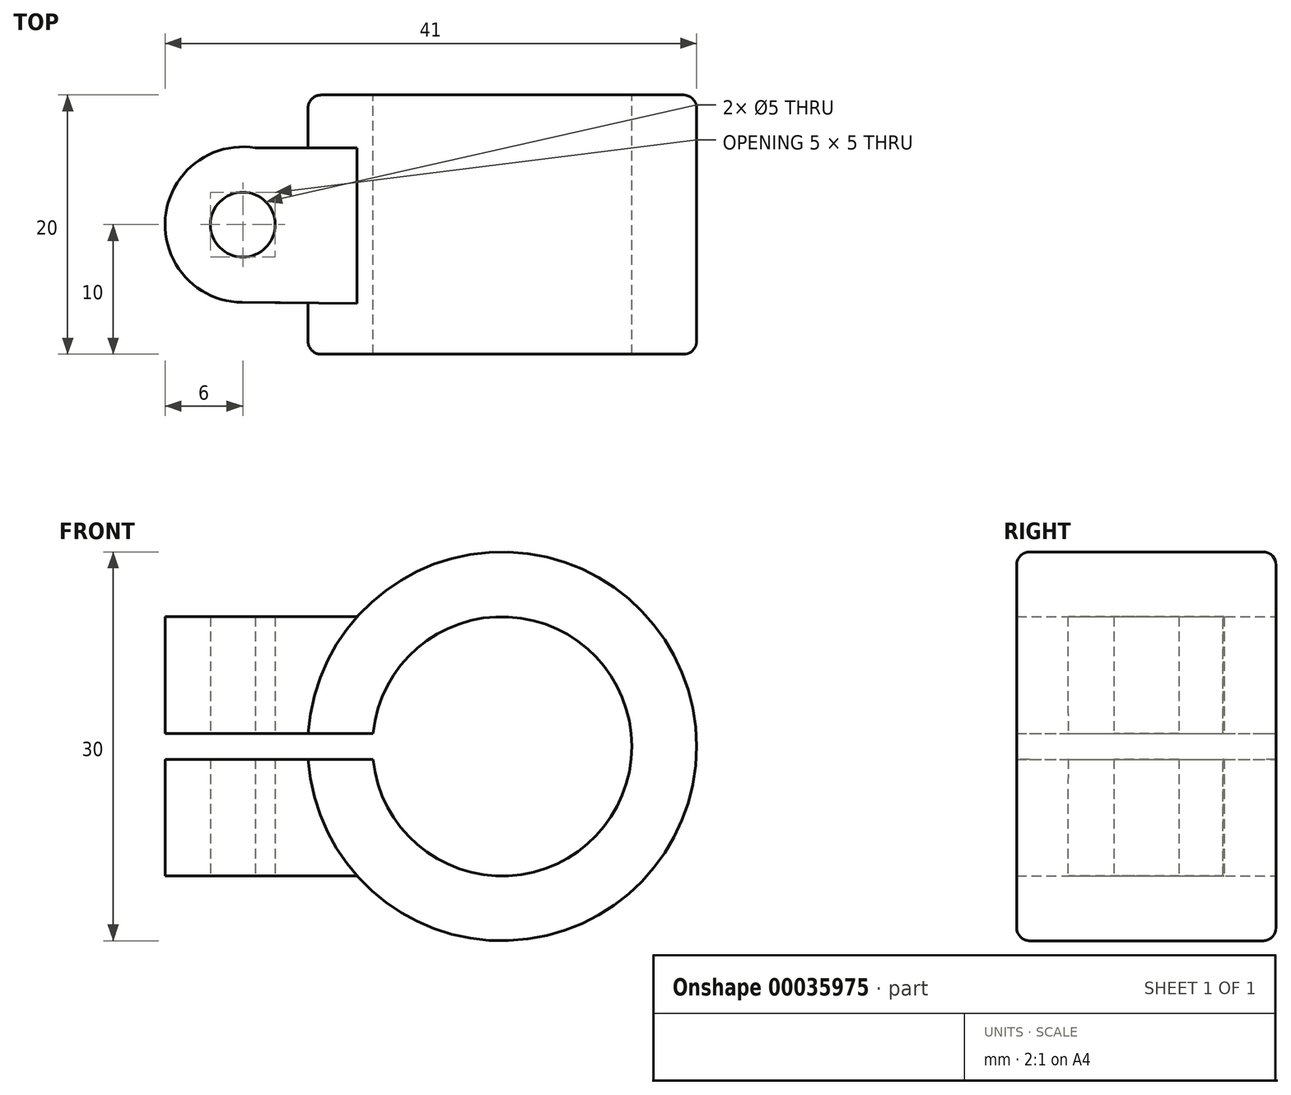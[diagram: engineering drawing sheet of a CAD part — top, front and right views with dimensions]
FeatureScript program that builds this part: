
annotation { "Feature Type Name" : "Feature", "Feature Type Description" : "" }
export const myFeature = defineFeature(function(context is Context, id is Id, definition is map)
    precondition{}
    {
        {
            var Q0;
            Q0=qCreatedBy(makeId("Front.planeOp"),FACE);
            var sketch = newSketch(context, id + "F0", { "sketchPlane" : qUnion([Q0])});
            skCircle(sketch, "E0", {"center": v(0, 0) * mm, "radius": 10 * mm});
            skCircle(sketch, "E1", {"center": v(0, 0) * mm, "radius": 15 * mm});
            skSolve(sketch);
        }
        {
            var Q0;
            Q0=makeQuery(id+"F0.imprint","IMPRINT",FACE,{"disambiguationData":[TD([[makeQuery(id+"F0.imprint","IMPRINT",EDGE,{"derivedFrom":sQuery(id+"F0.wireOp",EDGE,"E0")}),-1.0]])]});
            extrude(context, id + "F1", {"entities" : qUnion([Q0]), "depth" : 10 * mm, "hasSecondDirection" : true, "secondDirectionOppositeDirection" : true, "secondDirectionDepth" : 10 * mm});
        }
        {
            var Q0;
            Q0=qCreatedBy(makeId("Top.planeOp"),FACE);
            var sketch = newSketch(context, id + "F2", { "sketchPlane" : qUnion([Q0])});
            skCircle(sketch, "E2", {"center": v(-20, 0) * mm, "radius": 2.5 * mm});
            skArc(sketch, "E3", {"start": v(-19.04, 5.92) * mm, "mid": v(-25.98, 0.5) * mm, "end": v(-20.05, -6) * mm});
            skLineSegment(sketch, "E4", {"start": v(-19.04, 5.92) * mm, "end": v(-11, 5.92) * mm});
            skLineSegment(sketch, "E5", {"start": v(-11, 5.92) * mm, "end": v(-11, -6.08) * mm});
            skLineSegment(sketch, "E6", {"start": v(-11, -6.08) * mm, "end": v(-20.05, -6) * mm});
            skPoint(sketch, "E7.orphan", {"position": v(-11, 0) * mm});
            skSolve(sketch);
        }
        {
            var Q0;
            Q0=makeQuery(id+"F2.imprint","IMPRINT",FACE,{"disambiguationData":[TD([[makeQuery(id+"F2.imprint","IMPRINT",EDGE,{"derivedFrom":sQuery(id+"F2.wireOp",EDGE,"E2")}),-1.0]])]});
            extrude(context, id + "F3", {"entities" : qUnion([Q0]), "operationType" : NewBodyOperationType.ADD, "depth" : 10 * mm, "hasSecondDirection" : true, "secondDirectionOppositeDirection" : true, "secondDirectionDepth" : 10 * mm});
        }
        {
            var Q0;
            Q0=qCreatedBy(makeId("Front.planeOp"),FACE);
            var sketch = newSketch(context, id + "F4", { "sketchPlane" : qUnion([Q0])});
            skLineSegment(sketch, "E8.bottom", {"start": v(-56.6, 1) * mm, "end": v(-6.6, 1) * mm});
            skLineSegment(sketch, "E8.top", {"start": v(-56.6, -1) * mm, "end": v(-6.6, -1) * mm});
            skLineSegment(sketch, "E8.left", {"start": v(-56.6, 1) * mm, "end": v(-56.6, -1) * mm});
            skLineSegment(sketch, "E8.right", {"start": v(-6.6, 1) * mm, "end": v(-6.6, -1) * mm});
            skSolve(sketch);
        }
        {
            var Q0;
            Q0=makeQuery(id+"F4.imprint","IMPRINT",FACE,{"disambiguationData":[TD([[makeQuery(id+"F4.imprint","IMPRINT",EDGE,{"derivedFrom":sQuery(id+"F4.wireOp",EDGE,"E8.bottom")}),-1.0]])]});
            extrude(context, id + "F5", {"entities" : qUnion([Q0]), "operationType" : NewBodyOperationType.REMOVE, "oppositeDirection" : true, "depth" : 25 * mm, "hasSecondDirection" : true, "secondDirectionOppositeDirection" : false, "secondDirectionDepth" : 25 * mm});
        }
        {
            var Q0;
            Q0=makeQuery(id+"F1.opExtrude","CAP_EDGE",EDGE,{"disambiguationData":[OSD([sQuery(id+"F0.wireOp",EDGE,"E1")])],"isStart":false});
            var Q1;
            Q1=makeQuery(id+"F1.opExtrude","CAP_EDGE",EDGE,{"disambiguationData":[OSD([sQuery(id+"F0.wireOp",EDGE,"E1")])],"isStart":true});
            fillet(context, id + "F6", {"entities" : qUnion([Q0, Q1]), "radius" : 1 * mm, "tangentPropagation" : true, "allowEdgeOverflow" : false});
        }
    });
